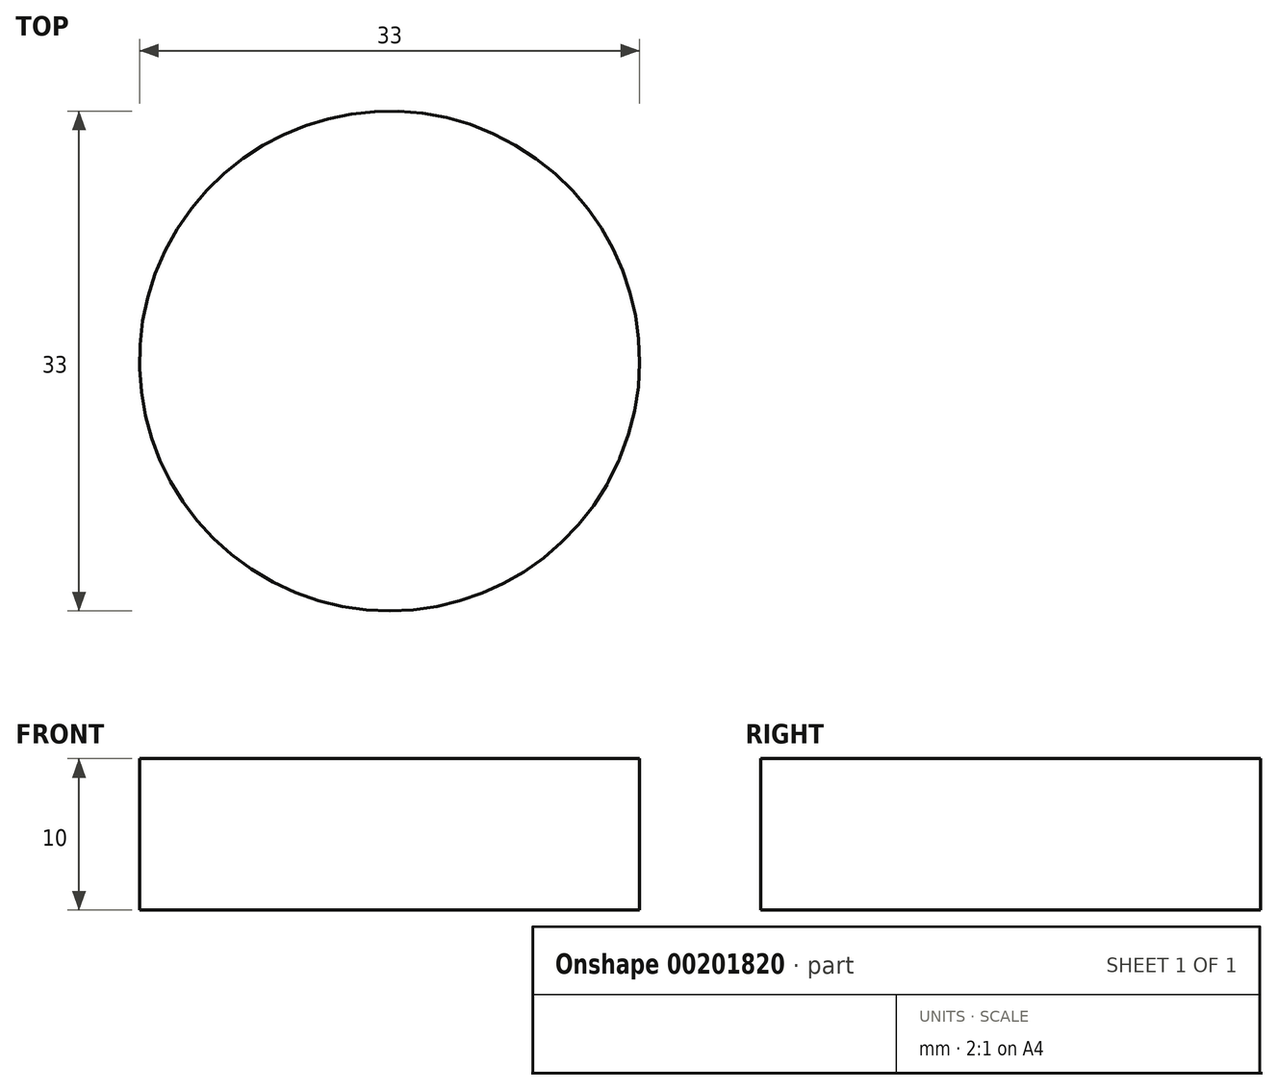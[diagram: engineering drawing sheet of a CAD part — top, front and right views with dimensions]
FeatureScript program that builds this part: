
annotation { "Feature Type Name" : "Feature", "Feature Type Description" : "" }
export const myFeature = defineFeature(function(context is Context, id is Id, definition is map)
    precondition{}
    {
        {
            var Q0;
            Q0=qCreatedBy(makeId("Top.planeOp"),FACE);
            var sketch = newSketch(context, id + "F0", { "sketchPlane" : qUnion([Q0])});
            skCircle(sketch, "E0", {"center": v(0, 0) * mm, "radius": 16.5 * mm});
            skLineSegment(sketch, "E1", {"start": v(-15.16, -6.52) * mm, "end": v(0, -37.34) * mm});
            skLineSegment(sketch, "E2", {"start": v(0, -2.33) * mm, "end": v(0, -37.34) * mm, "construction": true});
            skLineSegment(sketch, "E3.MirrorCS", {"start": v(15.16, -6.52) * mm, "end": v(0, -37.34) * mm});
            skSolve(sketch);
        }
        {
            var Q0;
            {var subQ0=sQuery(id+"F0.wireOp",EDGE,"E1");var subQ1=sQuery(id+"F0.wireOp",EDGE,"E0");var subQ2=makeQuery(id+"F0.imprint","INTERSECT",VERTEX,{"disambiguationData":[OD(0.0)],"derivedFrom":[subQ1,subQ0]});Q0=makeQuery(id+"F0.imprint","IMPRINT",FACE,{"disambiguationData":[TD([[makeQuery(id+"F0.imprint","IMPRINT",EDGE,{"disambiguationData":[TD([[subQ2,-1.0]])],"derivedFrom":subQ1}),1.0]])]});}
            var Q1;
            {var subQ0=sQuery(id+"F0.wireOp",EDGE,"E1");var subQ1=sQuery(id+"F0.wireOp",EDGE,"E0");var subQ2=makeQuery(id+"F0.imprint","INTERSECT",VERTEX,{"disambiguationData":[OD(1.0)],"derivedFrom":[subQ1,subQ0]});Q1=makeQuery(id+"F0.imprint","IMPRINT",FACE,{"disambiguationData":[TD([[makeQuery(id+"F0.imprint","IMPRINT",EDGE,{"disambiguationData":[TD([[subQ2,-1.0]])],"derivedFrom":subQ1}),-1.0]])]});}
            var Q2;
            {var subQ0=sQuery(id+"F0.wireOp",EDGE,"E3.MirrorCS");var subQ1=sQuery(id+"F0.wireOp",EDGE,"E0");var subQ2=makeQuery(id+"F0.imprint","INTERSECT",VERTEX,{"disambiguationData":[OD(0.0)],"derivedFrom":[subQ1,subQ0]});Q2=makeQuery(id+"F0.imprint","IMPRINT",FACE,{"disambiguationData":[TD([[makeQuery(id+"F0.imprint","IMPRINT",EDGE,{"disambiguationData":[TD([[subQ2,1.0]])],"derivedFrom":subQ1}),1.0]])]});}
            var Q3;
            {var subQ0=sQuery(id+"F0.wireOp",EDGE,"E1");var subQ1=sQuery(id+"F0.wireOp",EDGE,"E0");var subQ2=makeQuery(id+"F0.imprint","INTERSECT",VERTEX,{"disambiguationData":[OD(1.0)],"derivedFrom":[subQ1,subQ0]});Q3=makeQuery(id+"F0.imprint","IMPRINT",FACE,{"disambiguationData":[TD([[makeQuery(id+"F0.imprint","IMPRINT",EDGE,{"disambiguationData":[TD([[subQ2,-1.0]])],"derivedFrom":subQ1}),1.0]])]});}
            extrude(context, id + "F1", {"entities" : qUnion([Q0, Q1, Q2, Q3]), "depth" : 10 * mm});
        }
        {
            var Q0;
            Q0=makeQuery(id+"F1.opExtrude","SWEPT_EDGE",EDGE,{"disambiguationData":[OSD([sQuery(id+"F0.wireOp",EDGE,"E1"),sQuery(id+"F0.wireOp",EDGE,"E3.MirrorCS")])]});
            fillet(context, id + "F2", {"entities" : qUnion([Q0]), "radius" : 4 * mm, "tangentPropagation" : true, "allowEdgeOverflow" : false});
        }
    });
